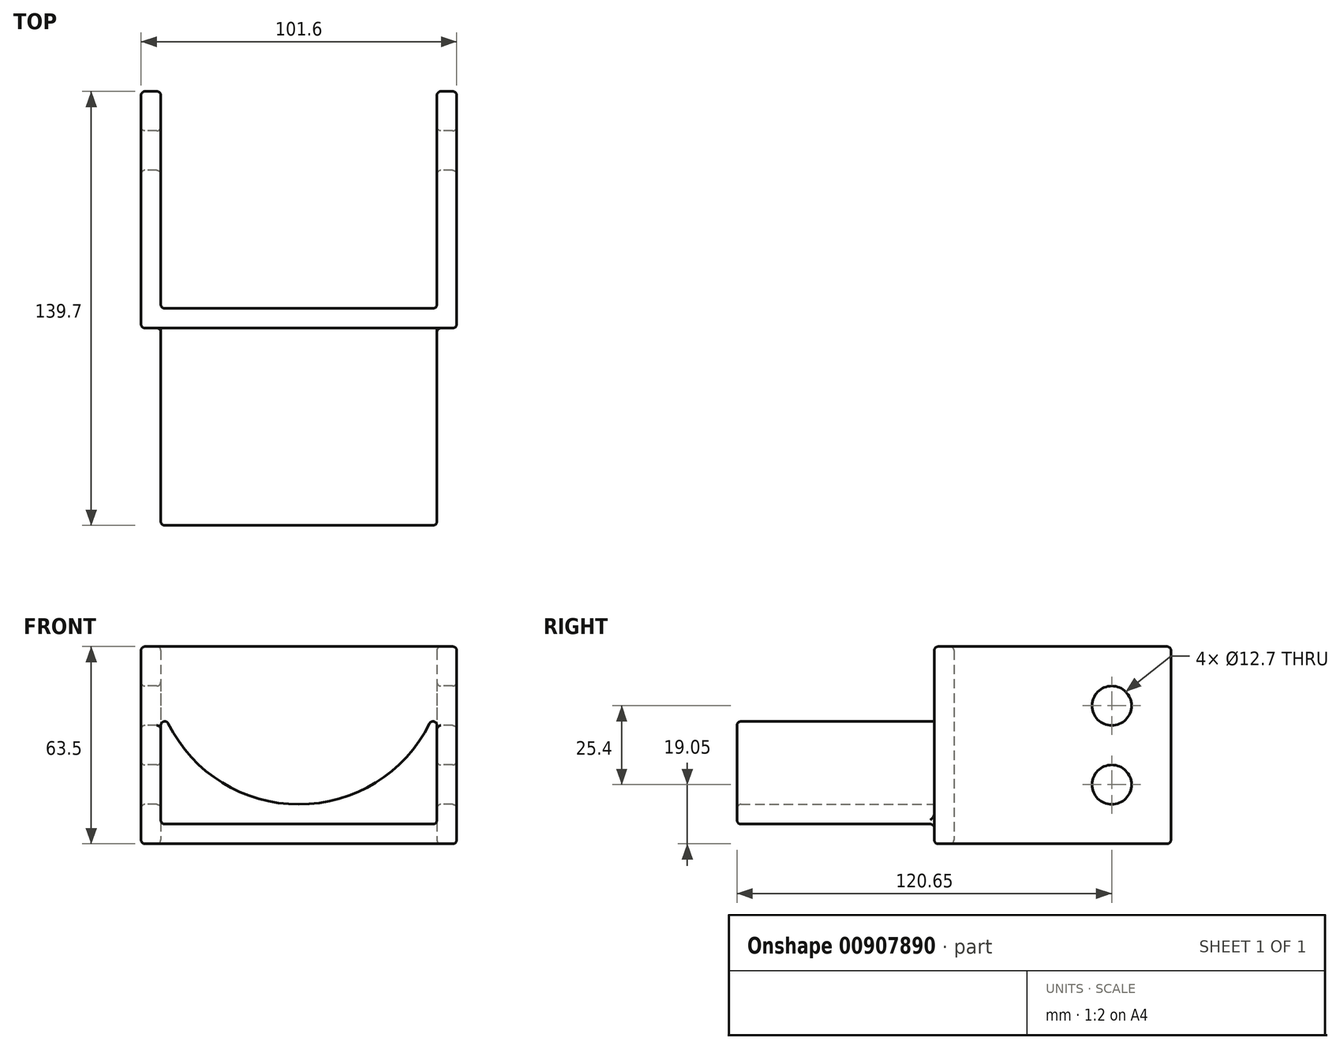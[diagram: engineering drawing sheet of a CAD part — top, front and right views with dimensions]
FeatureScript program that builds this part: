
annotation { "Feature Type Name" : "Feature", "Feature Type Description" : "" }
export const myFeature = defineFeature(function(context is Context, id is Id, definition is map)
    precondition{}
    {
        {
            var Q0;
            Q0=qCreatedBy(makeId("Top.planeOp"),FACE);
            var sketch = newSketch(context, id + "F0", { "sketchPlane" : qUnion([Q0])});
            skLineSegment(sketch, "E0.bottom", {"start": v(0, 0) * mm, "end": v(101.6, 0) * mm});
            skLineSegment(sketch, "E0.top", {"start": v(0, 76.2) * mm, "end": v(101.6, 76.2) * mm});
            skLineSegment(sketch, "E0.left", {"start": v(0, 0) * mm, "end": v(0, 76.2) * mm});
            skLineSegment(sketch, "E0.right", {"start": v(101.6, 0) * mm, "end": v(101.6, 76.2) * mm});
            skSolve(sketch);
        }
        {
            var Q0;
            Q0=makeQuery(id+"F0.imprint","IMPRINT",FACE,{"disambiguationData":[TD([[makeQuery(id+"F0.imprint","IMPRINT",EDGE,{"derivedFrom":sQuery(id+"F0.wireOp",EDGE,"E0.bottom")}),1.0]])]});
            extrude(context, id + "F1", {"entities" : qUnion([Q0]), "depth" : 63.5 * mm, "offsetDistance" : 25.4 * mm});
        }
        {
            var Q0;
            Q0=makeQuery(id+"F1.opExtrude","CAP_FACE",FACE,{"disambiguationData":[OSD([sQuery(id+"F0.wireOp",EDGE,"E0.bottom"),sQuery(id+"F0.wireOp",EDGE,"E0.top"),sQuery(id+"F0.wireOp",EDGE,"E0.left"),sQuery(id+"F0.wireOp",EDGE,"E0.right")])],"isStart":false});
            var Q1;
            Q1=makeQuery(id+"F1.opExtrude","SWEPT_FACE",FACE,{"disambiguationData":[OSD([sQuery(id+"F0.wireOp",EDGE,"E0.top")])]});
            var Q2;
            Q2=makeQuery(id+"F1.opExtrude","CAP_FACE",FACE,{"disambiguationData":[OSD([sQuery(id+"F0.wireOp",EDGE,"E0.bottom"),sQuery(id+"F0.wireOp",EDGE,"E0.top"),sQuery(id+"F0.wireOp",EDGE,"E0.left"),sQuery(id+"F0.wireOp",EDGE,"E0.right")])],"isStart":true});
            shell(context, id + "F2", {"entities" : qUnion([Q0, Q1, Q2]), "thickness" : 6.35 * mm});
        }
        {
            var Q0;
            Q0=makeQuery(id+"F1.opExtrude","SWEPT_FACE",FACE,{"disambiguationData":[OSD([sQuery(id+"F0.wireOp",EDGE,"E0.bottom")])]});
            var sketch = newSketch(context, id + "F3", { "sketchPlane" : qUnion([Q0])});
            skLineSegment(sketch, "E1.top", {"start": v(6.35, 6.35) * mm, "end": v(95.25, 6.35) * mm});
            skLineSegment(sketch, "E1.left", {"start": v(6.35, 44.45) * mm, "end": v(6.35, 6.35) * mm});
            skLineSegment(sketch, "E1.right", {"start": v(95.25, 44.45) * mm, "end": v(95.25, 6.35) * mm});
            skArc(sketch, "E2", {"start": v(6.35, 44.45) * mm, "mid": v(50.8, 12.7) * mm, "end": v(95.25, 44.45) * mm});
            skSolve(sketch);
        }
        {
            var Q0;
            Q0=makeQuery(id+"F3.imprint","IMPRINT",FACE,{"disambiguationData":[TD([[makeQuery(id+"F3.imprint","IMPRINT",EDGE,{"derivedFrom":sQuery(id+"F3.wireOp",EDGE,"E1.top")}),1.0]])]});
            extrude(context, id + "F4", {"entities" : qUnion([Q0]), "operationType" : NewBodyOperationType.ADD, "depth" : 63.5 * mm, "offsetDistance" : 25.4 * mm});
        }
        {
            var Q0;
            Q0=makeQuery(id+"F1.opExtrude","SWEPT_FACE",FACE,{"disambiguationData":[OSD([sQuery(id+"F0.wireOp",EDGE,"E0.left")])]});
            var Q1;
            Q1=makeQuery(id+"F4.opExtrude","SWEPT_EDGE",EDGE,{"disambiguationData":[OSD([sQuery(id+"F3.wireOp",EDGE,"E1.right"),sQuery(id+"F3.wireOp",EDGE,"E2")])]});
            var Q2;
            Q2=makeQuery(id+"F4.opExtrude","SWEPT_EDGE",EDGE,{"disambiguationData":[OSD([sQuery(id+"F3.wireOp",EDGE,"E1.left"),sQuery(id+"F3.wireOp",EDGE,"E2")])]});
            var Q3;
            Q3=makeQuery(id+"F4.opExtrude","CAP_FACE",FACE,{"disambiguationData":[OSD([sQuery(id+"F3.wireOp",EDGE,"E1.top"),sQuery(id+"F3.wireOp",EDGE,"E1.left"),sQuery(id+"F3.wireOp",EDGE,"E1.right"),sQuery(id+"F3.wireOp",EDGE,"E2")])],"isStart":false});
            var Q4;
            Q4=makeQuery(id+"F1.opExtrude","CAP_FACE",FACE,{"disambiguationData":[OSD([sQuery(id+"F0.wireOp",EDGE,"E0.bottom"),sQuery(id+"F0.wireOp",EDGE,"E0.top"),sQuery(id+"F0.wireOp",EDGE,"E0.left"),sQuery(id+"F0.wireOp",EDGE,"E0.right")])],"isStart":false});
            var Q5;
            Q5=makeQuery(id+"F1.opExtrude","SWEPT_FACE",FACE,{"disambiguationData":[OSD([sQuery(id+"F0.wireOp",EDGE,"E0.right")])]});
            var Q6;
            Q6=makeQuery(id+"F2.opShell","OFFSET_FACE",FACE,{"disambiguationData":[OSD([sQuery(id+"F0.wireOp",EDGE,"E0.left")])]});
            var Q7;
            Q7=makeQuery(id+"F2.opShell","OFFSET_FACE",FACE,{"disambiguationData":[OSD([sQuery(id+"F0.wireOp",EDGE,"E0.bottom")])]});
            var Q8;
            Q8=makeQuery(id+"F2.opShell","OFFSET_FACE",FACE,{"disambiguationData":[OSD([sQuery(id+"F0.wireOp",EDGE,"E0.right")])]});
            var Q9;
            Q9=makeQuery(id+"F1.opExtrude","CAP_FACE",FACE,{"disambiguationData":[OSD([sQuery(id+"F0.wireOp",EDGE,"E0.bottom"),sQuery(id+"F0.wireOp",EDGE,"E0.top"),sQuery(id+"F0.wireOp",EDGE,"E0.left"),sQuery(id+"F0.wireOp",EDGE,"E0.right")])],"isStart":true});
            var Q10;
            Q10=makeQuery(id+"F4.opExtrude","SWEPT_FACE",FACE,{"disambiguationData":[OSD([sQuery(id+"F3.wireOp",EDGE,"E1.top")])]});
            fillet(context, id + "F5", {"entities" : qUnion([Q0, Q1, Q2, Q3, Q4, Q5, Q6, Q7, Q8, Q9, Q10]), "radius" : 1.27 * mm, "tangentPropagation" : true, "allowEdgeOverflow" : false});
        }
        {
            var Q0;
            Q0=makeQuery(id+"F1.opExtrude","SWEPT_FACE",FACE,{"disambiguationData":[OSD([sQuery(id+"F0.wireOp",EDGE,"E0.left")])]});
            var sketch = newSketch(context, id + "F6", { "sketchPlane" : qUnion([Q0])});
            skCircle(sketch, "E3", {"center": v(-57.15, 44.45) * mm, "radius": 6.35 * mm});
            skCircle(sketch, "E4", {"center": v(-57.15, 19.05) * mm, "radius": 6.35 * mm});
            skSolve(sketch);
        }
        {
            var Q0;
            Q0=makeQuery(id+"F6.imprint","IMPRINT",FACE,{"disambiguationData":[TD([[makeQuery(id+"F6.imprint","IMPRINT",EDGE,{"derivedFrom":sQuery(id+"F6.wireOp",EDGE,"E3")}),1.0]])]});
            var Q1;
            Q1=makeQuery(id+"F6.imprint","IMPRINT",FACE,{"disambiguationData":[TD([[makeQuery(id+"F6.imprint","IMPRINT",EDGE,{"derivedFrom":sQuery(id+"F6.wireOp",EDGE,"E4")}),1.0]])]});
            extrude(context, id + "F7", {"entities" : qUnion([Q0, Q1]), "operationType" : NewBodyOperationType.REMOVE, "endBound" : BoundingType.THROUGH_ALL, "oppositeDirection" : true, "depth" : 25.4 * mm, "offsetDistance" : 25.4 * mm});
        }
        {
            var Q0;
            {var subQ0=sQuery(id+"F0.wireOp",EDGE,"E0.left");Q0=makeQuery(id+"F7.boolean.opBoolean","COPY",FACE,{"disambiguationData":[TD([makeQuery(id+"F1.opExtrude","SWEPT_FACE",FACE,{"disambiguationData":[OSD([subQ0])]})])],"derivedFrom":makeQuery(id+"F7.opExtrude","SWEPT_FACE",FACE,{"disambiguationData":[OSD([sQuery(id+"F6.wireOp",EDGE,"E3")])]})});}
            var Q1;
            {var subQ0=sQuery(id+"F0.wireOp",EDGE,"E0.left");Q1=makeQuery(id+"F7.boolean.opBoolean","COPY",FACE,{"disambiguationData":[TD([makeQuery(id+"F1.opExtrude","SWEPT_FACE",FACE,{"disambiguationData":[OSD([subQ0])]})])],"derivedFrom":makeQuery(id+"F7.opExtrude","SWEPT_FACE",FACE,{"disambiguationData":[OSD([sQuery(id+"F6.wireOp",EDGE,"E4")])]})});}
            var Q2;
            {var subQ0=sQuery(id+"F0.wireOp",EDGE,"E0.right");Q2=makeQuery(id+"F7.boolean.opBoolean","COPY",FACE,{"disambiguationData":[TD([makeQuery(id+"F1.opExtrude","SWEPT_FACE",FACE,{"disambiguationData":[OSD([subQ0])]})])],"derivedFrom":makeQuery(id+"F7.opExtrude","SWEPT_FACE",FACE,{"disambiguationData":[OSD([sQuery(id+"F6.wireOp",EDGE,"E3")])]})});}
            var Q3;
            {var subQ0=sQuery(id+"F0.wireOp",EDGE,"E0.right");Q3=makeQuery(id+"F7.boolean.opBoolean","COPY",FACE,{"disambiguationData":[TD([makeQuery(id+"F1.opExtrude","SWEPT_FACE",FACE,{"disambiguationData":[OSD([subQ0])]})])],"derivedFrom":makeQuery(id+"F7.opExtrude","SWEPT_FACE",FACE,{"disambiguationData":[OSD([sQuery(id+"F6.wireOp",EDGE,"E4")])]})});}
            fillet(context, id + "F8", {"entities" : qUnion([Q0, Q1, Q2, Q3]), "radius" : 1.27 * mm, "tangentPropagation" : true, "allowEdgeOverflow" : false});
        }
    });
